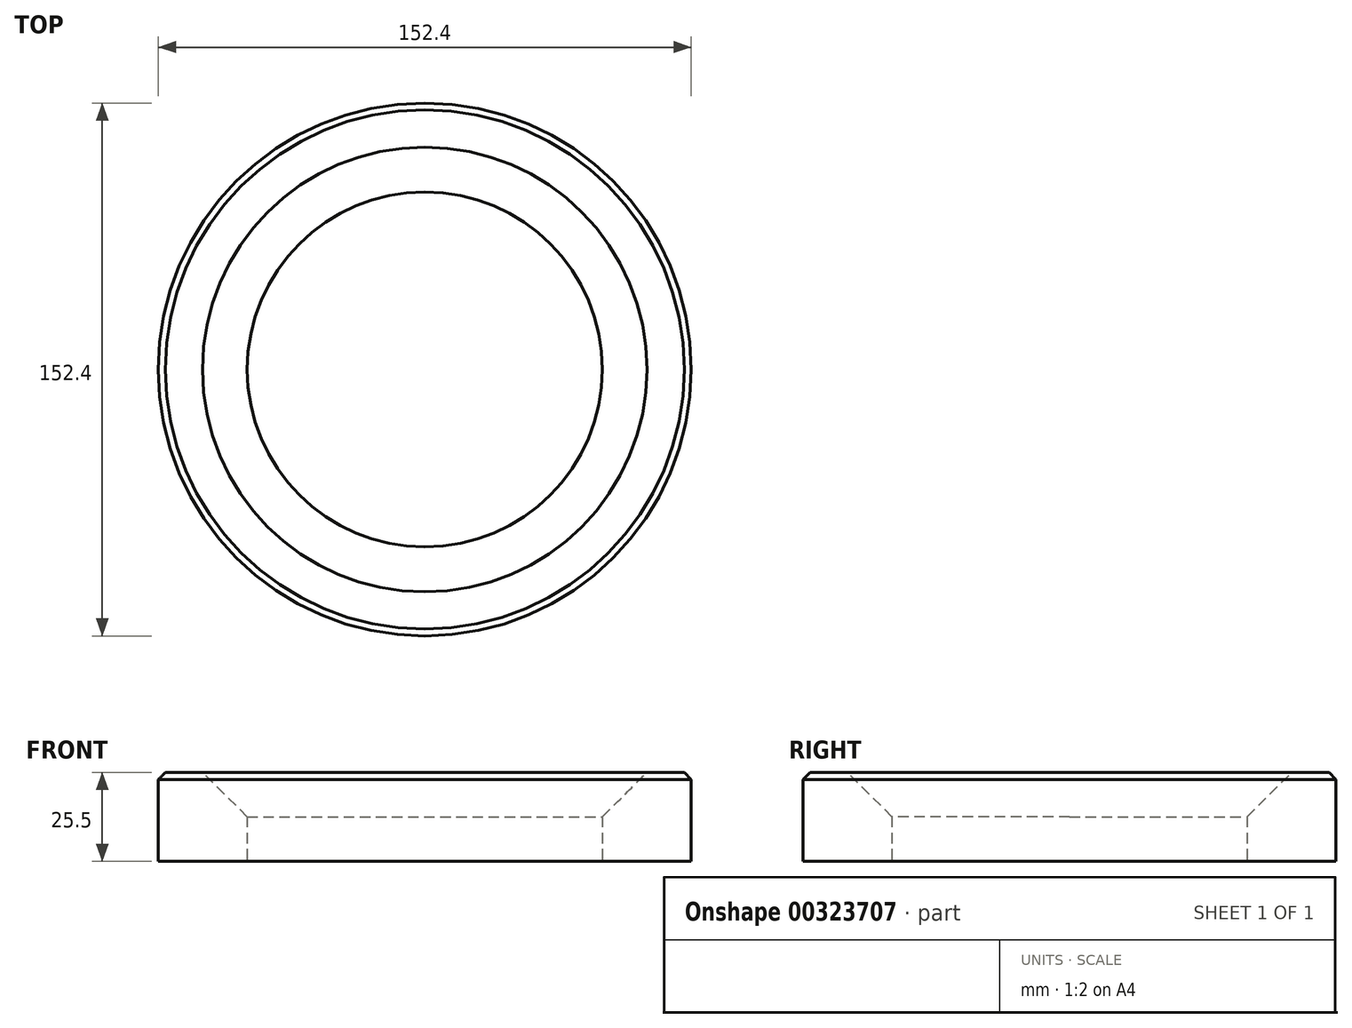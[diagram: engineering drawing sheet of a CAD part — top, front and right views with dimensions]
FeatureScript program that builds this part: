
annotation { "Feature Type Name" : "Feature", "Feature Type Description" : "" }
export const myFeature = defineFeature(function(context is Context, id is Id, definition is map)
    precondition{}
    {
        {
            var Q0;
            Q0=qCreatedBy(makeId("Front.planeOp"),FACE);
            var sketch = newSketch(context, id + "F0", { "sketchPlane" : qUnion([Q0])});
            skLineSegment(sketch, "E0", {"start": v(0, 0) * mm, "end": v(76.2, 0) * mm});
            skLineSegment(sketch, "E1", {"start": v(76.2, 0) * mm, "end": v(76.2, 0) * mm});
            skLineSegment(sketch, "E2", {"start": v(76.2, 0) * mm, "end": v(76.2, 25.4) * mm});
            skLineSegment(sketch, "E3", {"start": v(50.8, 0) * mm, "end": v(50.76, 25.6) * mm});
            skLineSegment(sketch, "E4", {"start": v(0, 0) * mm, "end": v(0, 41.92) * mm, "construction": true});
            skLineSegment(sketch, "E5", {"start": v(50.76, 25.6) * mm, "end": v(76.2, 25.4) * mm});
            skSolve(sketch);
        }
        {
            var Q0;
            {var subQ0=sQuery(id+"F0.wireOp",EDGE,"E2");Q0=makeQuery(id+"F0.imprint","IMPRINT",FACE,{"disambiguationData":[TD([[makeQuery(id+"F0.imprint","IMPRINT",EDGE,{"derivedFrom":subQ0}),1.0]])]});}
            var Q1;
            Q1=sQuery(id+"F0.wireOp",EDGE,"E4");
            revolve(context, id + "F1", {"entities" : qUnion([Q0]), "axis" : qUnion([Q1]), "revolveType" : RevolveType.FULL});
        }
        {
            var Q0;
            Q0=makeQuery(id+"F1.opRevolve","SWEPT_EDGE",EDGE,{"disambiguationData":[OSD([sQuery(id+"F0.wireOp",EDGE,"E3"),sQuery(id+"F0.wireOp",EDGE,"E5")])]});
            chamfer(context, id + "F2", {"entities" : qUnion([Q0]), "width" : 12.7 * mm, "tangentPropagation" : true});
        }
        {
            var Q0;
            Q0=makeQuery(id+"F1.opRevolve","SWEPT_EDGE",EDGE,{"disambiguationData":[OSD([sQuery(id+"F0.wireOp",EDGE,"E2"),sQuery(id+"F0.wireOp",EDGE,"E5")])]});
            chamfer(context, id + "F3", {"entities" : qUnion([Q0]), "width" : 2 * mm, "tangentPropagation" : true});
        }
    });
